# Revit family: BVN_ARMO-C
name_source: partatom
category: Mechanical Equipment
units: mm (PartAtom-declared; Revit-internal decimal feet)

## family parameters
Cut with Voids When Loaded = No
Host = Face
Part Type = Normal
Room Calculation Point = No
Round Connector Dimension = Use Diameter
Shared = No

## types (21) — shared parameters
Default Elevation = 1219 mm
Description = Smoke Exhaust Fan
Manufacturer = Bahçıvan Elektrik Motor San. ve Tic. Ltd. Şti.
Material = <By Category>
Model = ARMO-C
URL = http://www.bahcivanmotor.com.tr
x = 50 mm  [stored 0.164042 ft]

## per-type parameters (varying)
| type | A | Air Flow | B | Current | H | HH' | L | L' | L'' | Power | Q | QD | QD' | Speed(d/d) | W | Wing Angle (Degree) | a | b | y |
| ARMO-C 400-6/1,5-2A | 490 mm  [stored 1.60761 ft] | 8978 m³/h | 490 mm  [stored 1.60761 ft] | 3 A | 640 mm | 72 mm  [stored 0.23622 ft] | 592 mm  [stored 1.94226 ft] | 246 mm  [stored 0.807087 ft] | -246 mm  [stored -0.807087 ft] | 1500 W | 390 mm  [stored 1.27953 ft] | 148 mm  [stored 0.485564 ft] | -148 mm  [stored -0.485564 ft] | 2900 | 568 mm  [stored 1.86352 ft] | 30 | 39 mm  [stored 0.127953 ft] | 39 mm  [stored 0.127953 ft] | 36 mm |
| ARMO-C 450-6/3-2A | 490 mm  [stored 1.60761 ft] | 13545 m³/h | 490 mm  [stored 1.60761 ft] | 6 A | 640 mm | 72 mm  [stored 0.23622 ft] | 592 mm  [stored 1.94226 ft] | 246 mm  [stored 0.807087 ft] | -246 mm  [stored -0.807087 ft] | 3000 W | 390 mm  [stored 1.27953 ft] | 148 mm  [stored 0.485564 ft] | -148 mm  [stored -0.485564 ft] | 2900 | 568 mm  [stored 1.86352 ft] | 28 | 39 mm  [stored 0.127953 ft] | 39 mm  [stored 0.127953 ft] | 36 mm |
| ARMO-C 500-6/4-2A | 536 mm | 17325 m³/h | 536 mm | 7 A | 686 mm | 66 mm | 592 mm  [stored 1.94226 ft] | 246 mm  [stored 0.807087 ft] | -246 mm  [stored -0.807087 ft] | 4000 W | 436 mm  [stored 1.43045 ft] | 148 mm  [stored 0.485564 ft] | -148 mm  [stored -0.485564 ft] | 2900 | 620 mm  [stored 2.03412 ft] | 26 | 42 mm | 42 mm | 33 mm |
| ARMO-C 560-6/7,5-2A | 624 mm  [stored 2.04724 ft] | 25725 m³/h | 624 mm  [stored 2.04724 ft] | 13 A | 775 mm | 68 mm | 745 mm | 323 mm | -323 mm | 7500 W | 524 mm  [stored 1.71916 ft] | 186 mm  [stored 0.610236 ft] | -186 mm  [stored -0.610236 ft] | 2800 | 707 mm | 24 | 42 mm | 42 mm | 34 mm |
| ARMO-C 710-6/4-4A | 774 mm | 31500 m³/h | 774 mm | 8 A | 925 mm | 68 mm | 910 mm | 405 mm | -405 mm | 4000 W | 674 mm | 228 mm | -228 mm | 1415 | 857 mm | 32 | 42 mm | 42 mm | 34 mm |
| ARMO-C 800-9/11-4A | 865 mm | 29400 m³/h | 865 mm | 8 A | 1025 mm | 75 mm | 910 mm | 405 mm | -405 mm | 4000 W | 765 mm | 228 mm | -228 mm | 1415 | 950 mm | 20 | 43 mm | 43 mm | 38 mm |
| ARMO-C 900-9/15-4A | 965 mm | 63525 m³/h | 965 mm | 29 A | 1125 mm | 75 mm | 1065 mm | 483 mm | -483 mm | 15000 W | 865 mm | 266 mm | -266 mm | 1450 | 1050 mm | 32 | 43 mm | 43 mm | 38 mm |
| ARMO-C 1000-9/30-4A | 1069 mm | 86100 m³/h | 1069 mm | 55 A | 1250 mm | 100 mm  [stored 0.328084 ft] | 1065 mm | 483 mm | -483 mm | 30000 W | 969 mm | 266 mm | -266 mm | 1460 | 1150 mm | 32 | 41 mm | 41 mm | 50 mm  [stored 0.164042 ft] |
| ARMO-C 1250-9/45-4A | 1319 mm | 138800 m³/h | 1319 mm | 80 A | 1500 mm | 100 mm  [stored 0.328084 ft] | 1065 mm | 483 mm | -483 mm | 45000 W | 1219 mm | 266 mm | -266 mm | 1475 | 1400 mm | 24 | 41 mm | 41 mm | 50 mm  [stored 0.164042 ft] |
| ARMO-C 630-6/5,5-2A | 694 mm | 20475 m³/h | 694 mm | 11 A | 845 mm | 68 mm | 745 mm | 323 mm | -323 mm | 5500 W | 594 mm | 186 mm  [stored 0.610236 ft] | -186 mm  [stored -0.610236 ft] | 2900 | 777 mm | 10 | 42 mm | 42 mm | 34 mm |
| ARMO-C 500-6/1,1-4A | 536 mm | 12600 m³/h | 536 mm | 3 A | 686 mm | 66 mm | 592 mm  [stored 1.94226 ft] | 246 mm  [stored 0.807087 ft] | -246 mm  [stored -0.807087 ft] | 1100 W | 436 mm  [stored 1.43045 ft] | 148 mm  [stored 0.485564 ft] | -148 mm  [stored -0.485564 ft] | 1400 | 620 mm  [stored 2.03412 ft] | 38 | 42 mm | 42 mm | 33 mm |
| ARMO-C 560-6/2,2-4A | 624 mm  [stored 2.04724 ft] | 17850 m³/h | 624 mm  [stored 2.04724 ft] | 5 A | 775 mm | 68 mm | 745 mm | 323 mm | -323 mm | 2200 W | 524 mm  [stored 1.71916 ft] | 186 mm  [stored 0.610236 ft] | -186 mm  [stored -0.610236 ft] | 1410 | 707 mm | 38 | 42 mm | 42 mm | 34 mm |
| ARMO-C 630-6/3-4A | 694 mm | 24150 m³/h | 694 mm | 7 A | 845 mm | 68 mm | 745 mm | 323 mm | -323 mm | 3000 W | 594 mm | 186 mm  [stored 0.610236 ft] | -186 mm  [stored -0.610236 ft] | 1410 | 777 mm | 36 | 42 mm | 42 mm | 34 mm |
| ARMO-C 500-6/0.37-6A | 536 mm | 8400 m³/h | 536 mm | 1 A | 686 mm | 66 mm | 592 mm  [stored 1.94226 ft] | 246 mm  [stored 0.807087 ft] | -246 mm  [stored -0.807087 ft] | 370 W | 436 mm  [stored 1.43045 ft] | 148 mm  [stored 0.485564 ft] | -148 mm  [stored -0.485564 ft] | 900 | 620 mm  [stored 2.03412 ft] | 38 | 42 mm | 42 mm | 33 mm |
| ARMO-C 560-6/0,55-6A | 624 mm  [stored 2.04724 ft] | 13650 m³/h | 624 mm  [stored 2.04724 ft] | 2 A | 775 mm | 68 mm | 745 mm | 323 mm | -323 mm | 550 W | 524 mm  [stored 1.71916 ft] | 186 mm  [stored 0.610236 ft] | -186 mm  [stored -0.610236 ft] | 930 | 707 mm | 28 | 42 mm | 42 mm | 34 mm |
| ARMO-C 630-6/1,1-6A | 694 mm | 16800 m³/h | 694 mm | 3 A | 845 mm | 68 mm | 745 mm | 323 mm | -323 mm | 1100 W | 594 mm | 186 mm  [stored 0.610236 ft] | -186 mm  [stored -0.610236 ft] | 945 | 777 mm | 38 | 42 mm | 42 mm | 34 mm |
| ARMO-C 710-6/4-6A | 774 mm | 21000 m³/h | 774 mm | 9 A | 925 mm | 68 mm | 910 mm | 405 mm | -405 mm | 4000 W | 674 mm | 228 mm | -228 mm | 955 | 857 mm | 32 | 42 mm | 42 mm | 34 mm |
| ARMO-C 800-9/3-6A | 865 mm | 28350 m³/h | 865 mm | 7 A | 1025 mm | 75 mm | 910 mm | 405 mm | -405 mm | 3000 W | 765 mm | 228 mm | -228 mm | 950 | 950 mm | 32 | 43 mm | 43 mm | 38 mm |
| ARMO-C 900-9/4-6A | 965 mm | 39900 m³/h | 965 mm | 9 A | 1125 mm | 75 mm | 1065 mm | 483 mm | -483 mm | 4000 W | 865 mm | 266 mm | -266 mm | 955 | 1050 mm | 30 | 43 mm | 43 mm | 38 mm |
| ARMO-C 1000-9/7,5-6A | 1069 mm | 57750 m³/h | 1069 mm | 15 A | 1250 mm | 100 mm  [stored 0.328084 ft] | 1065 mm | 483 mm | -483 mm | 5500 W | 969 mm | 266 mm | -266 mm | 960 | 1150 mm | 32 | 41 mm | 41 mm | 50 mm  [stored 0.164042 ft] |
| ARMO-C 1250-9/15-6A | 1319 mm | 105000 m³/h | 1319 mm | 29 A | 1500 mm | 100 mm  [stored 0.328084 ft] | 1065 mm | 483 mm | -483 mm | 15000 W | 1219 mm | 266 mm | -266 mm | 965 | 1400 mm | 28 | 41 mm | 41 mm | 50 mm  [stored 0.164042 ft] |

note: [stored X ft] marks values corroborated as IEEE doubles in the binary element streams (Revit-internal decimal feet)

## geometry (parser evidence)
native form markers: Sweep x2
no freeform markers — native parametric forms only
